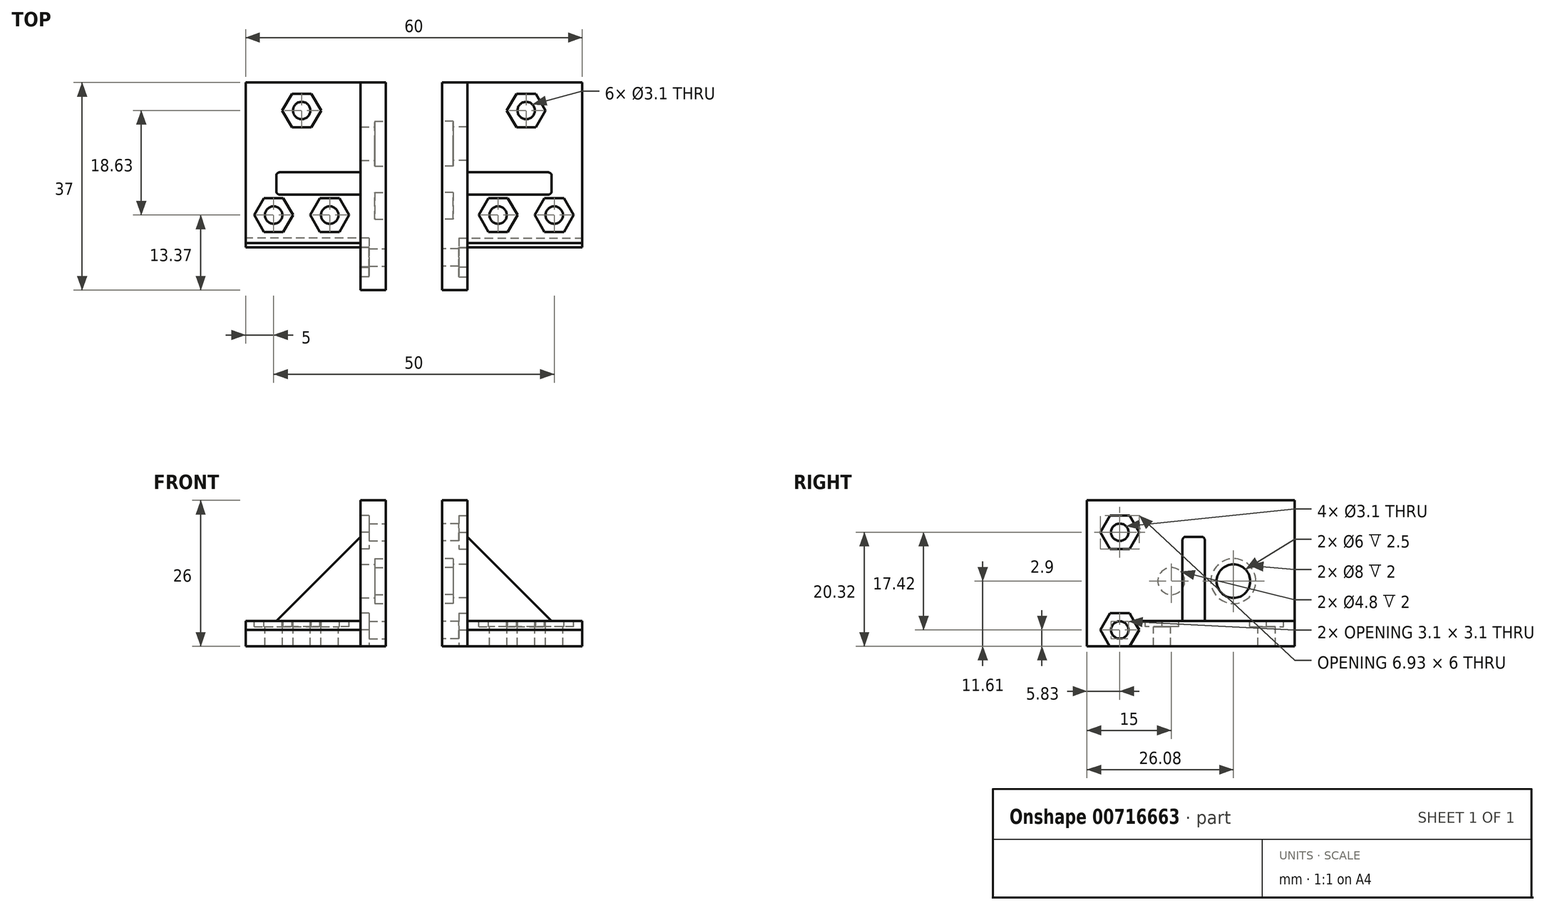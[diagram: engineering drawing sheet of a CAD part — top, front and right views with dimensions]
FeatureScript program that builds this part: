
annotation { "Feature Type Name" : "Feature", "Feature Type Description" : "" }
export const myFeature = defineFeature(function(context is Context, id is Id, definition is map)
    precondition{}
    {
        {
            var Q0;
            Q0=qCreatedBy(makeId("Front.planeOp"),FACE);
            var sketch = newSketch(context, id + "F0", { "sketchPlane" : qUnion([Q0])});
            skLineSegment(sketch, "E0", {"start": v(0, 0) * mm, "end": v(0, 26) * mm});
            skLineSegment(sketch, "E1", {"start": v(0, 26) * mm, "end": v(4.5, 26) * mm});
            skLineSegment(sketch, "E2", {"start": v(0, 0) * mm, "end": v(25, 0) * mm});
            skLineSegment(sketch, "E3", {"start": v(25, 0) * mm, "end": v(25, 4.5) * mm});
            skLineSegment(sketch, "E4", {"start": v(25, 4.5) * mm, "end": v(4.5, 4.5) * mm});
            skLineSegment(sketch, "E5", {"start": v(4.5, 4.5) * mm, "end": v(4.5, 26) * mm});
            skLineSegment(sketch, "E6", {"start": v(4.5, 19.5) * mm, "end": v(19.5, 4.5) * mm});
            skSolve(sketch);
        }
        {
            var Q0;
            Q0=makeQuery(id+"F0.imprint","IMPRINT",FACE,{"disambiguationData":[TD([[makeQuery(id+"F0.imprint","IMPRINT",EDGE,{"derivedFrom":sQuery(id+"F0.wireOp",EDGE,"E0")}),-1.0]])]});
            extrude(context, id + "F1", {"entities" : qUnion([Q0]), "depth" : 19 * mm, "offsetDistance" : 25 * mm, "hasSecondDirection" : true, "secondDirectionOppositeDirection" : true, "secondDirectionDepth" : 18 * mm});
        }
        {
            var Q0;
            {var subQ3=sQuery(id+"F0.wireOp",EDGE,"E6");Q0=makeQuery(id+"F0.imprint","IMPRINT",FACE,{"disambiguationData":[TD([[makeQuery(id+"F0.imprint","IMPRINT",EDGE,{"derivedFrom":subQ3}),-1.0]])]});}
            extrude(context, id + "F2", {"entities" : qUnion([Q0]), "operationType" : NewBodyOperationType.ADD, "depth" : 2 * mm, "offsetDistance" : 25 * mm, "hasSecondDirection" : true, "secondDirectionOppositeDirection" : true, "secondDirectionDepth" : 2 * mm});
        }
        {
            var Q0;
            Q0=makeQuery(id+"F1.opExtrude","SWEPT_FACE",FACE,{"disambiguationData":[OSD([sQuery(id+"F0.wireOp",EDGE,"E0")])]});
            var sketch = newSketch(context, id + "F3", { "sketchPlane" : qUnion([Q0])});
            skCircle(sketch, "E7", {"center": v(13.17, 2.9) * mm, "radius": 1.55 * mm});
            skCircle(sketch, "E8", {"center": v(13.17, 20.32) * mm, "radius": 1.55 * mm});
            skCircle(sketch, "E9", {"center": v(4, 11.61) * mm, "radius": 2.4 * mm});
            skCircle(sketch, "E10", {"center": v(-7.08, 11.61) * mm, "radius": 4 * mm});
            skCircle(sketch, "E11", {"center": v(-7.08, 11.61) * mm, "radius": 3 * mm});
            skSolve(sketch);
        }
        {
            var Q0;
            Q0=makeQuery(id+"F3.imprint","IMPRINT",FACE,{"disambiguationData":[TD([[makeQuery(id+"F3.imprint","IMPRINT",EDGE,{"derivedFrom":sQuery(id+"F3.wireOp",EDGE,"E7")}),1.0]])]});
            var Q1;
            Q1=makeQuery(id+"F3.imprint","IMPRINT",FACE,{"disambiguationData":[TD([[makeQuery(id+"F3.imprint","IMPRINT",EDGE,{"derivedFrom":sQuery(id+"F3.wireOp",EDGE,"E8")}),1.0]])]});
            extrude(context, id + "F4", {"entities" : qUnion([Q0, Q1]), "operationType" : NewBodyOperationType.REMOVE, "oppositeDirection" : true, "depth" : 26 * mm, "offsetDistance" : 25 * mm});
        }
        {
            var Q0;
            Q0=makeQuery(id+"F1.opExtrude","SWEPT_FACE",FACE,{"disambiguationData":[OSD([sQuery(id+"F0.wireOp",EDGE,"E3")])]});
            var sketch = newSketch(context, id + "F5", { "sketchPlane" : qUnion([Q0])});
            skCircle(sketch, "E12.cCircle", {"center": v(-13.17, 2.9) * mm, "radius": 3 * mm, "construction": true});
            skLineSegment(sketch, "E12.0", {"start": v(-11.44, -0.1) * mm, "end": v(-14.9, -0.1) * mm});
            skLineSegment(sketch, "E12.1", {"start": v(-14.9, -0.1) * mm, "end": v(-16.63, 2.9) * mm});
            skLineSegment(sketch, "E12.2", {"start": v(-16.63, 2.9) * mm, "end": v(-14.9, 5.9) * mm});
            skLineSegment(sketch, "E12.3", {"start": v(-14.9, 5.9) * mm, "end": v(-11.44, 5.9) * mm});
            skLineSegment(sketch, "E12.4", {"start": v(-11.44, 5.9) * mm, "end": v(-9.7, 2.9) * mm});
            skLineSegment(sketch, "E12.5", {"start": v(-9.7, 2.9) * mm, "end": v(-11.44, -0.1) * mm});
            skPoint(sketch, "E12.0.midPoint", {"position": v(-13.17, -0.1) * mm});
            skCircle(sketch, "E13.cCircle", {"center": v(-13.17, 20.32) * mm, "radius": 3 * mm, "construction": true});
            skLineSegment(sketch, "E13.0", {"start": v(-11.44, 17.32) * mm, "end": v(-14.9, 17.32) * mm});
            skLineSegment(sketch, "E13.1", {"start": v(-14.9, 17.32) * mm, "end": v(-16.63, 20.32) * mm});
            skLineSegment(sketch, "E13.2", {"start": v(-16.63, 20.32) * mm, "end": v(-14.9, 23.32) * mm});
            skLineSegment(sketch, "E13.3", {"start": v(-14.9, 23.32) * mm, "end": v(-11.44, 23.32) * mm});
            skLineSegment(sketch, "E13.4", {"start": v(-11.44, 23.32) * mm, "end": v(-9.7, 20.32) * mm});
            skLineSegment(sketch, "E13.5", {"start": v(-9.7, 20.32) * mm, "end": v(-11.44, 17.32) * mm});
            skPoint(sketch, "E13.0.midPoint", {"position": v(-13.17, 17.32) * mm});
            skLineSegment(sketch, "E14.bottom", {"start": v(-19, 0) * mm, "end": v(-14.52, 0) * mm});
            skLineSegment(sketch, "E14.top", {"start": v(-19, 4.5) * mm, "end": v(-14.52, 4.5) * mm});
            skLineSegment(sketch, "E14.left", {"start": v(-19, 0) * mm, "end": v(-19, 4.5) * mm});
            skLineSegment(sketch, "E14.right", {"start": v(-14.52, 0) * mm, "end": v(-14.52, 4.5) * mm});
            skSolve(sketch);
        }
        {
            var Q0;
            Q0=makeQuery(id+"F5.imprint","IMPRINT",FACE,{"disambiguationData":[TD([[makeQuery(id+"F5.imprint","IMPRINT",EDGE,{"derivedFrom":sQuery(id+"F5.wireOp",EDGE,"E13.0")}),-1.0]])]});
            var Q1;
            {var subQ6=sQuery(id+"F5.wireOp",EDGE,"E12.0");Q1=makeQuery(id+"F5.imprint","IMPRINT",FACE,{"disambiguationData":[TD([[makeQuery(id+"F5.imprint","IMPRINT",EDGE,{"derivedFrom":subQ6}),-1.0]])]});}
            var Q2;
            {var subQ1=sQuery(id+"F5.wireOp",EDGE,"E12.3");Q2=makeQuery(id+"F5.imprint","IMPRINT",FACE,{"disambiguationData":[TD([[makeQuery(id+"F5.imprint","IMPRINT",EDGE,{"derivedFrom":subQ1}),-1.0]])]});}
            var Q3;
            {var subQ4=sQuery(id+"F5.wireOp",EDGE,"E12.2");var subQ6=sQuery(id+"F5.wireOp",EDGE,"E12.1");var subQ7=makeQuery(id+"F5.imprint","INTERSECT",VERTEX,{"derivedFrom":[subQ6,subQ4]});Q3=makeQuery(id+"F5.imprint","IMPRINT",FACE,{"disambiguationData":[TD([[makeQuery(id+"F5.imprint","IMPRINT",EDGE,{"disambiguationData":[TD([[subQ7,1.0]])],"derivedFrom":subQ6}),-1.0]])]});}
            var Q4;
            {var subQ9=sQuery(id+"F5.wireOp",EDGE,"E12.5");var subQ10=sQuery(id+"F5.wireOp",EDGE,"E12.4");var subQ11=makeQuery(id+"F5.imprint","INTERSECT",VERTEX,{"derivedFrom":[subQ10,subQ9]});Q4=makeQuery(id+"F5.imprint","IMPRINT",FACE,{"disambiguationData":[TD([[makeQuery(id+"F5.imprint","IMPRINT",EDGE,{"disambiguationData":[TD([[subQ11,1.0]])],"derivedFrom":subQ10}),-1.0]])]});}
            var Q5;
            {var subQ0=sQuery(id+"F5.wireOp",EDGE,"E14.right");var subQ1=makeQuery(id+"F4.boolean.opBoolean","INTERSECT",EDGE,{"derivedFrom":[makeQuery(id+"F1.opExtrude","SWEPT_FACE",FACE,{"disambiguationData":[OSD([sQuery(id+"F0.wireOp",EDGE,"E3")])]}),makeQuery(id+"F4.opExtrude","SWEPT_FACE",FACE,{"disambiguationData":[OSD([sQuery(id+"F3.wireOp",EDGE,"E7")])]})]});var subQ2=makeQuery(id+"F5.imprint","INTERSECT",VERTEX,{"disambiguationData":[OD(0.0)],"derivedFrom":[subQ1,subQ0]});Q5=makeQuery(id+"F5.imprint","IMPRINT",FACE,{"disambiguationData":[TD([[makeQuery(id+"F5.imprint","IMPRINT",EDGE,{"disambiguationData":[TD([[subQ2,-1.0]])],"derivedFrom":subQ0}),1.0]])]});}
            var Q6;
            {var subQ0=sQuery(id+"F5.wireOp",EDGE,"E14.right");var subQ1=makeQuery(id+"F4.boolean.opBoolean","INTERSECT",EDGE,{"derivedFrom":[makeQuery(id+"F1.opExtrude","SWEPT_FACE",FACE,{"disambiguationData":[OSD([sQuery(id+"F0.wireOp",EDGE,"E3")])]}),makeQuery(id+"F4.opExtrude","SWEPT_FACE",FACE,{"disambiguationData":[OSD([sQuery(id+"F3.wireOp",EDGE,"E7")])]})]});var subQ2=makeQuery(id+"F5.imprint","INTERSECT",VERTEX,{"disambiguationData":[OD(0.0)],"derivedFrom":[subQ1,subQ0]});Q6=makeQuery(id+"F5.imprint","IMPRINT",FACE,{"disambiguationData":[TD([[makeQuery(id+"F5.imprint","IMPRINT",EDGE,{"disambiguationData":[TD([[subQ2,-1.0]])],"derivedFrom":subQ0}),-1.0]])]});}
            extrude(context, id + "F6", {"entities" : qUnion([Q0, Q1, Q2, Q3, Q4, Q5, Q6]), "operationType" : NewBodyOperationType.REMOVE, "oppositeDirection" : true, "depth" : 22 * mm, "offsetDistance" : 25 * mm});
        }
        {
            var Q0;
            {var subQ2=sQuery(id+"F0.wireOp",EDGE,"E3");Q0=makeQuery(id+"F6.boolean.opBoolean","SPLIT",FACE,{"disambiguationData":[TD([makeQuery(id+"F6.opExtrude","SWEPT_FACE",FACE,{"disambiguationData":[OSD([sQuery(id+"F5.wireOp",EDGE,"E12.1")])]})])],"derivedFrom":makeQuery(id+"F1.opExtrude","SWEPT_FACE",FACE,{"disambiguationData":[OSD([subQ2])]})});}
            extrude(context, id + "F7", {"entities" : qUnion([Q0]), "operationType" : NewBodyOperationType.REMOVE, "oppositeDirection" : true, "depth" : 20.5 * mm, "offsetDistance" : 25 * mm});
        }
        {
            var Q0;
            {var subQ0=sQuery(id+"F0.wireOp",EDGE,"E6");var subQ2=sQuery(id+"F0.wireOp",EDGE,"E4");Q0=makeQuery(id+"F6.boolean.opBoolean","SPLIT",FACE,{"disambiguationData":[TD([makeQuery(id+"F2.opExtrude","SWEPT_FACE",FACE,{"disambiguationData":[OSD([subQ0])]})])],"derivedFrom":makeQuery(id+"F1.opExtrude","SWEPT_FACE",FACE,{"disambiguationData":[OSD([subQ2])]})});}
            var sketch = newSketch(context, id + "F8", { "sketchPlane" : qUnion([Q0])});
            skCircle(sketch, "E15", {"center": v(20, -5.63) * mm, "radius": 1.55 * mm});
            skCircle(sketch, "E16", {"center": v(10, -5.63) * mm, "radius": 1.55 * mm});
            skCircle(sketch, "E17", {"center": v(15, 13) * mm, "radius": 1.55 * mm});
            skCircle(sketch, "E18.cCircle", {"center": v(10, -5.63) * mm, "radius": 3 * mm, "construction": true});
            skLineSegment(sketch, "E18.0", {"start": v(11.73, -8.63) * mm, "end": v(8.27, -8.63) * mm});
            skLineSegment(sketch, "E18.1", {"start": v(8.27, -8.63) * mm, "end": v(6.54, -5.63) * mm});
            skLineSegment(sketch, "E18.2", {"start": v(6.54, -5.63) * mm, "end": v(8.27, -2.63) * mm});
            skLineSegment(sketch, "E18.3", {"start": v(8.27, -2.63) * mm, "end": v(11.73, -2.63) * mm});
            skLineSegment(sketch, "E18.4", {"start": v(11.73, -2.63) * mm, "end": v(13.46, -5.63) * mm});
            skLineSegment(sketch, "E18.5", {"start": v(13.46, -5.63) * mm, "end": v(11.73, -8.63) * mm});
            skPoint(sketch, "E18.0.midPoint", {"position": v(10, -8.63) * mm});
            skCircle(sketch, "E19.cCircle", {"center": v(20, -5.63) * mm, "radius": 3 * mm, "construction": true});
            skLineSegment(sketch, "E19.0", {"start": v(21.73, -8.63) * mm, "end": v(18.27, -8.63) * mm});
            skLineSegment(sketch, "E19.1", {"start": v(18.27, -8.63) * mm, "end": v(16.54, -5.63) * mm});
            skLineSegment(sketch, "E19.2", {"start": v(16.54, -5.63) * mm, "end": v(18.27, -2.63) * mm});
            skLineSegment(sketch, "E19.3", {"start": v(18.27, -2.63) * mm, "end": v(21.73, -2.63) * mm});
            skLineSegment(sketch, "E19.4", {"start": v(21.73, -2.63) * mm, "end": v(23.46, -5.63) * mm});
            skLineSegment(sketch, "E19.5", {"start": v(23.46, -5.63) * mm, "end": v(21.73, -8.63) * mm});
            skPoint(sketch, "E19.0.midPoint", {"position": v(20, -8.63) * mm});
            skCircle(sketch, "E20.cCircle", {"center": v(15, 13) * mm, "radius": 3 * mm, "construction": true});
            skLineSegment(sketch, "E20.0", {"start": v(13.27, 16) * mm, "end": v(16.73, 16) * mm});
            skLineSegment(sketch, "E20.1", {"start": v(16.73, 16) * mm, "end": v(18.46, 13) * mm});
            skLineSegment(sketch, "E20.2", {"start": v(18.46, 13) * mm, "end": v(16.73, 10) * mm});
            skLineSegment(sketch, "E20.3", {"start": v(16.73, 10) * mm, "end": v(13.27, 10) * mm});
            skLineSegment(sketch, "E20.4", {"start": v(13.27, 10) * mm, "end": v(11.54, 13) * mm});
            skLineSegment(sketch, "E20.5", {"start": v(11.54, 13) * mm, "end": v(13.27, 16) * mm});
            skPoint(sketch, "E20.0.midPoint", {"position": v(15, 16) * mm});
            skSolve(sketch);
        }
        {
            var Q0;
            Q0 = qSketchRegion(id + "F8", true);
            var Q1;
            Q1=makeQuery(id+"F8.imprint","IMPRINT",FACE,{"disambiguationData":[TD([[makeQuery(id+"F8.imprint","IMPRINT",EDGE,{"derivedFrom":sQuery(id+"F8.wireOp",EDGE,"E16")}),1.0]])]});
            var Q2;
            Q2=makeQuery(id+"F8.imprint","IMPRINT",FACE,{"disambiguationData":[TD([[makeQuery(id+"F8.imprint","IMPRINT",EDGE,{"derivedFrom":sQuery(id+"F8.wireOp",EDGE,"E15")}),1.0]])]});
            var Q3;
            Q3=makeQuery(id+"F8.imprint","IMPRINT",FACE,{"disambiguationData":[TD([[makeQuery(id+"F8.imprint","IMPRINT",EDGE,{"derivedFrom":sQuery(id+"F8.wireOp",EDGE,"E17")}),1.0]])]});
            extrude(context, id + "F9", {"entities" : qUnion([Q0, Q1, Q2, Q3]), "operationType" : NewBodyOperationType.REMOVE, "oppositeDirection" : true, "depth" : 1 * mm, "offsetDistance" : 25 * mm});
        }
        {
            var Q0;
            Q0=makeQuery(id+"F8.imprint","IMPRINT",FACE,{"disambiguationData":[TD([[makeQuery(id+"F8.imprint","IMPRINT",EDGE,{"derivedFrom":sQuery(id+"F8.wireOp",EDGE,"E16")}),1.0]])]});
            var Q1;
            Q1=makeQuery(id+"F8.imprint","IMPRINT",FACE,{"disambiguationData":[TD([[makeQuery(id+"F8.imprint","IMPRINT",EDGE,{"derivedFrom":sQuery(id+"F8.wireOp",EDGE,"E15")}),1.0]])]});
            var Q2;
            Q2=makeQuery(id+"F8.imprint","IMPRINT",FACE,{"disambiguationData":[TD([[makeQuery(id+"F8.imprint","IMPRINT",EDGE,{"derivedFrom":sQuery(id+"F8.wireOp",EDGE,"E17")}),1.0]])]});
            extrude(context, id + "F10", {"entities" : qUnion([Q0, Q1, Q2]), "operationType" : NewBodyOperationType.REMOVE, "oppositeDirection" : true, "depth" : 6 * mm, "offsetDistance" : 25 * mm});
        }
        {
            var Q0;
            Q0=makeQuery(id+"F2.opExtrude","CAP_EDGE",EDGE,{"disambiguationData":[OSD([sQuery(id+"F0.wireOp",EDGE,"E6")])],"isStart":false});
            var Q1;
            Q1=makeQuery(id+"F2.opExtrude","CAP_EDGE",EDGE,{"disambiguationData":[OSD([sQuery(id+"F0.wireOp",EDGE,"E6")])],"isStart":true});
            fillet(context, id + "F11", {"entities" : qUnion([Q0, Q1]), "radius" : 0.5 * mm, "tangentPropagation" : true, "allowEdgeOverflow" : false});
        }
        {
            var Q0;
            Q0=makeQuery(id+"F3.imprint","IMPRINT",FACE,{"disambiguationData":[TD([[makeQuery(id+"F3.imprint","IMPRINT",EDGE,{"derivedFrom":sQuery(id+"F3.wireOp",EDGE,"E11")}),1.0]])]});
            extrude(context, id + "F12", {"entities" : qUnion([Q0]), "operationType" : NewBodyOperationType.REMOVE, "oppositeDirection" : true, "depth" : 6 * mm, "offsetDistance" : 25 * mm});
        }
        {
            var Q0;
            Q0=makeQuery(id+"F3.imprint","IMPRINT",FACE,{"disambiguationData":[TD([[makeQuery(id+"F3.imprint","IMPRINT",EDGE,{"derivedFrom":sQuery(id+"F3.wireOp",EDGE,"E10")}),1.0]])]});
            var Q1;
            Q1=makeQuery(id+"F3.imprint","IMPRINT",FACE,{"disambiguationData":[TD([[makeQuery(id+"F3.imprint","IMPRINT",EDGE,{"derivedFrom":sQuery(id+"F3.wireOp",EDGE,"E9")}),1.0]])]});
            extrude(context, id + "F13", {"entities" : qUnion([Q0, Q1]), "operationType" : NewBodyOperationType.REMOVE, "oppositeDirection" : true, "depth" : 2 * mm, "offsetDistance" : 25 * mm});
        }
        {
            var Q0;
            Q0=makeQuery(id+"F3.imprint","IMPRINT",FACE,{"disambiguationData":[TD([[makeQuery(id+"F3.imprint","IMPRINT",EDGE,{"derivedFrom":sQuery(id+"F3.wireOp",EDGE,"E7")}),-1.0]])]});
            cPlane(context, id + "F14", {"entities" : qUnion([Q0]), "cplaneType" : CPlaneType.OFFSET, "offset" : 5 * mm, "width" : 150 * mm, "height" : 150 * mm});
        }
        {
            var Q0;
            Q0=makeQuery(id+"F1.opExtrude","SWEPT_BODY",BODY,{"disambiguationData":[OSD([sQuery(id+"F0.wireOp",EDGE,"E0"),sQuery(id+"F0.wireOp",EDGE,"E1"),sQuery(id+"F0.wireOp",EDGE,"E2"),sQuery(id+"F0.wireOp",EDGE,"E3"),sQuery(id+"F0.wireOp",EDGE,"E4"),sQuery(id+"F0.wireOp",EDGE,"E5")])]});
            var Q1;
            Q1=qCreatedBy(id+"F14.planeOp",FACE);
            mirror(context, id + "F15", {"entities" : qUnion([Q0]), "mirrorPlane" : qUnion([Q1])});
        }
    });
